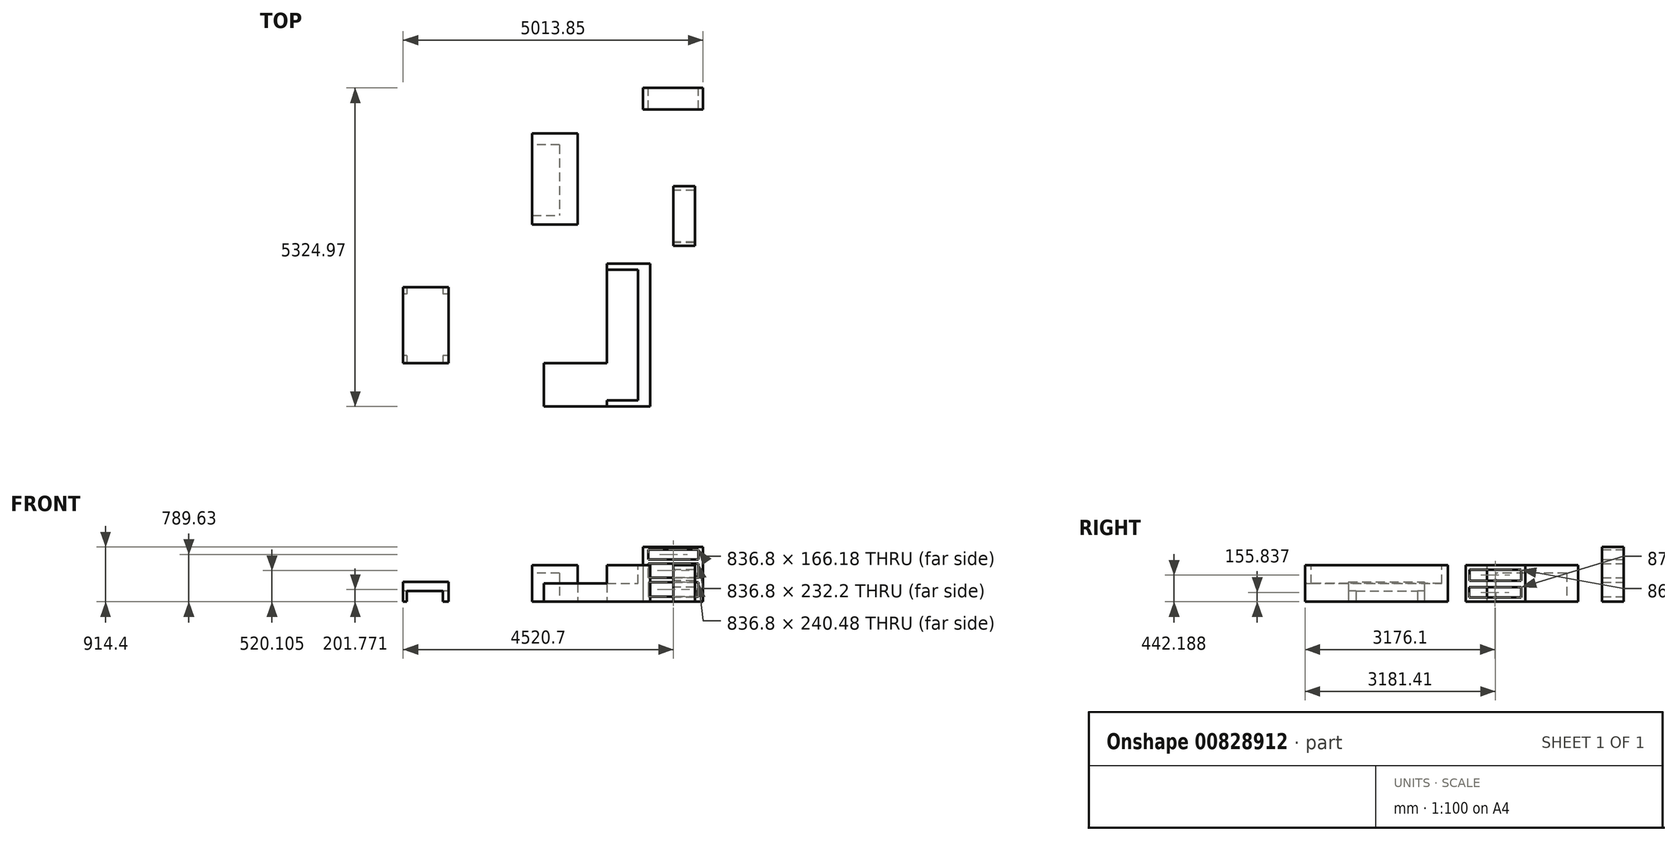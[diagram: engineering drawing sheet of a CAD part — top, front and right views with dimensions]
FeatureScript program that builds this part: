
annotation { "Feature Type Name" : "Feature", "Feature Type Description" : "" }
export const myFeature = defineFeature(function(context is Context, id is Id, definition is map)
    precondition{}
    {
        {
            var Q0;
            Q0=qCreatedBy(makeId("Top.planeOp"),FACE);
            var sketch = newSketch(context, id + "F0", { "sketchPlane" : qUnion([Q0])});
            skLineSegment(sketch, "E0", {"start": v(0, 0) * mm, "end": v(0, -723.9) * mm});
            skLineSegment(sketch, "E1", {"start": v(0, -723.9) * mm, "end": v(1778, -723.9) * mm});
            skLineSegment(sketch, "E2", {"start": v(1778, -723.9) * mm, "end": v(1778, 1663.7) * mm});
            skLineSegment(sketch, "E3", {"start": v(1778, 1663.7) * mm, "end": v(1054.1, 1663.7) * mm});
            skLineSegment(sketch, "E4", {"start": v(1054.1, 1663.7) * mm, "end": v(1054.1, 0) * mm});
            skLineSegment(sketch, "E5", {"start": v(1054.1, 0) * mm, "end": v(0, 0) * mm});
            skSolve(sketch);
        }
        {
            var Q0;
            Q0 = qSketchRegion(id + "F0", true);
            extrude(context, id + "F1", {"entities" : qUnion([Q0]), "depth" : 609.6 * mm, "offsetDistance" : 25.4 * mm});
        }
        {
            var Q0;
            Q0=makeQuery(id+"F1.opExtrude","CAP_FACE",FACE,{"disambiguationData":[OSD([sQuery(id+"F0.wireOp",EDGE,"E0"),sQuery(id+"F0.wireOp",EDGE,"E1"),sQuery(id+"F0.wireOp",EDGE,"E2"),sQuery(id+"F0.wireOp",EDGE,"E3"),sQuery(id+"F0.wireOp",EDGE,"E4"),sQuery(id+"F0.wireOp",EDGE,"E5")])],"isStart":false});
            var sketch = newSketch(context, id + "F2", { "sketchPlane" : qUnion([Q0])});
            skLineSegment(sketch, "E6", {"start": v(1054.1, -723.9) * mm, "end": v(1054.1, -622.3) * mm});
            skLineSegment(sketch, "E7", {"start": v(1054.1, -622.3) * mm, "end": v(1574.8, -622.3) * mm});
            skLineSegment(sketch, "E8", {"start": v(1574.8, -622.3) * mm, "end": v(1574.8, 1562.1) * mm});
            skLineSegment(sketch, "E9", {"start": v(1054.1, 0) * mm, "end": v(0, 0) * mm});
            skLineSegment(sketch, "E10", {"start": v(0, 0) * mm, "end": v(0, -723.9) * mm});
            skLineSegment(sketch, "E11", {"start": v(0, -723.9) * mm, "end": v(1054.1, -723.9) * mm});
            skLineSegment(sketch, "E12", {"start": v(1574.8, 1562.1) * mm, "end": v(1054.1, 1562.1) * mm});
            skLineSegment(sketch, "E13", {"start": v(1054.1, 0) * mm, "end": v(1054.1, 1562.1) * mm});
            skSolve(sketch);
        }
        {
            var Q0;
            Q0 = qSketchRegion(id + "F2", true);
            extrude(context, id + "F3", {"entities" : qUnion([Q0]), "operationType" : NewBodyOperationType.REMOVE, "oppositeDirection" : true, "depth" : 304.8 * mm, "offsetDistance" : 25.4 * mm});
        }
        {
            var Q0;
            Q0=qCreatedBy(makeId("Top.planeOp"),FACE);
            var sketch = newSketch(context, id + "F4", { "sketchPlane" : qUnion([Q0])});
            skLineSegment(sketch, "E14.bottom", {"start": v(-2356.13, 0) * mm, "end": v(-1594.13, 0) * mm});
            skLineSegment(sketch, "E14.top", {"start": v(-2356.13, 1270) * mm, "end": v(-1594.13, 1270) * mm});
            skLineSegment(sketch, "E14.left", {"start": v(-2356.13, 0) * mm, "end": v(-2356.13, 1270) * mm});
            skLineSegment(sketch, "E14.right", {"start": v(-1594.13, 0) * mm, "end": v(-1594.13, 1270) * mm});
            skSolve(sketch);
        }
        {
            var Q0;
            Q0 = qSketchRegion(id + "F4", true);
            extrude(context, id + "F5", {"entities" : qUnion([Q0]), "depth" : 330.2 * mm, "offsetDistance" : 25.4 * mm});
        }
        {
            var Q0;
            Q0=makeQuery(id+"F5.opExtrude","CAP_FACE",FACE,{"disambiguationData":[OSD([sQuery(id+"F4.wireOp",EDGE,"E14.bottom"),sQuery(id+"F4.wireOp",EDGE,"E14.top"),sQuery(id+"F4.wireOp",EDGE,"E14.left"),sQuery(id+"F4.wireOp",EDGE,"E14.right")])],"isStart":true});
            var sketch = newSketch(context, id + "F6", { "sketchPlane" : qUnion([Q0])});
            skLineSegment(sketch, "E15.bottom", {"start": v(-1594.13, -128.71) * mm, "end": v(-1690.59, -128.71) * mm});
            skLineSegment(sketch, "E15.top", {"start": v(-1594.13, -1156.15) * mm, "end": v(-1690.59, -1156.15) * mm});
            skLineSegment(sketch, "E15.left", {"start": v(-1594.13, -128.71) * mm, "end": v(-1594.13, -1156.15) * mm});
            skLineSegment(sketch, "E15.right", {"start": v(-2356.13, -128.71) * mm, "end": v(-2356.13, -1156.15) * mm});
            skLineSegment(sketch, "E16.bottom", {"start": v(-1690.59, -1270) * mm, "end": v(-2293.47, -1270) * mm});
            skLineSegment(sketch, "E16.top", {"start": v(-1690.59, 0) * mm, "end": v(-2293.47, 0) * mm});
            skLineSegment(sketch, "E16.left", {"start": v(-1690.59, -1270) * mm, "end": v(-1690.59, -1156.15) * mm});
            skLineSegment(sketch, "E16.right", {"start": v(-2293.47, -1270) * mm, "end": v(-2293.47, -1156.15) * mm});
            skLineSegment(sketch, "E17.trimOffspring", {"start": v(-1690.59, -128.71) * mm, "end": v(-1690.59, 0) * mm});
            skLineSegment(sketch, "E18.trimOffspring", {"start": v(-2293.47, -128.71) * mm, "end": v(-2356.13, -128.71) * mm});
            skLineSegment(sketch, "E19.trimOffspring", {"start": v(-2293.47, -128.71) * mm, "end": v(-2293.47, 0) * mm});
            skLineSegment(sketch, "E20.trimOffspring", {"start": v(-2293.47, -1156.15) * mm, "end": v(-2356.13, -1156.15) * mm});
            skSolve(sketch);
        }
        {
            var Q0;
            Q0 = qSketchRegion(id + "F6", true);
            extrude(context, id + "F7", {"entities" : qUnion([Q0]), "operationType" : NewBodyOperationType.REMOVE, "oppositeDirection" : true, "depth" : 177.8 * mm, "offsetDistance" : 25.4 * mm});
        }
        {
            var Q0;
            Q0=qCreatedBy(makeId("Top.planeOp"),FACE);
            var sketch = newSketch(context, id + "F8", { "sketchPlane" : qUnion([Q0])});
            skLineSegment(sketch, "E21.bottom", {"start": v(565.89, 2319.93) * mm, "end": v(-1059.71, 2319.93) * mm});
            skLineSegment(sketch, "E21.top", {"start": v(565.89, 3843.93) * mm, "end": v(-196.11, 3843.93) * mm});
            skLineSegment(sketch, "E21.left", {"start": v(565.89, 2319.93) * mm, "end": v(565.89, 3843.93) * mm});
            skLineSegment(sketch, "E21.right", {"start": v(-1059.71, 2319.93) * mm, "end": v(-1059.71, 2878.73) * mm});
            skLineSegment(sketch, "E22.top", {"start": v(-1059.71, 2878.73) * mm, "end": v(-196.11, 2878.73) * mm});
            skLineSegment(sketch, "E22.right", {"start": v(-196.11, 3843.93) * mm, "end": v(-196.11, 2878.73) * mm});
            skSolve(sketch);
        }
        {
            var Q0;
            Q0 = qSketchRegion(id + "F8", true);
            extrude(context, id + "F9", {"entities" : qUnion([Q0]), "depth" : 609.6 * mm, "offsetDistance" : 25.4 * mm});
        }
        {
            var Q0;
            Q0=makeQuery(id+"F9.opExtrude","SWEPT_FACE",FACE,{"disambiguationData":[OSD([sQuery(id+"F8.wireOp",EDGE,"E22.right")])]});
            var sketch = newSketch(context, id + "F10", { "sketchPlane" : qUnion([Q0])});
            skLineSegment(sketch, "E23.bottom", {"start": v(-3650.65, 479.96) * mm, "end": v(-2878.73, 479.96) * mm});
            skLineSegment(sketch, "E23.top", {"start": v(-3650.65, 0) * mm, "end": v(-2878.73, 0) * mm});
            skLineSegment(sketch, "E23.left", {"start": v(-3650.65, 479.96) * mm, "end": v(-3650.65, 0) * mm});
            skLineSegment(sketch, "E23.right", {"start": v(-2878.73, 479.96) * mm, "end": v(-2878.73, 0) * mm});
            skSolve(sketch);
        }
        {
            var Q0;
            Q0 = qSketchRegion(id + "F10", true);
            extrude(context, id + "F11", {"entities" : qUnion([Q0]), "operationType" : NewBodyOperationType.REMOVE, "oppositeDirection" : true, "depth" : 457.2 * mm, "offsetDistance" : 25.4 * mm});
        }
        {
            var Q0;
            Q0=makeQuery(id+"F11.boolean.opBoolean","MERGE",FACE,{"derivedFrom":[makeQuery(id+"F9.opExtrude","SWEPT_FACE",FACE,{"disambiguationData":[OSD([sQuery(id+"F8.wireOp",EDGE,"E22.top")])]}),makeQuery(id+"F11.opExtrude","SWEPT_FACE",FACE,{"disambiguationData":[OSD([sQuery(id+"F10.wireOp",EDGE,"E23.right")])]})]});
            var sketch = newSketch(context, id + "F12", { "sketchPlane" : qUnion([Q0])});
            skLineSegment(sketch, "E24.bottom", {"start": v(-261.09, 479.96) * mm, "end": v(509.69, 479.96) * mm});
            skLineSegment(sketch, "E24.top", {"start": v(-261.09, 0) * mm, "end": v(509.69, 0) * mm});
            skLineSegment(sketch, "E24.left", {"start": v(-261.09, 479.96) * mm, "end": v(-261.09, 0) * mm});
            skLineSegment(sketch, "E24.right", {"start": v(509.69, 479.96) * mm, "end": v(509.69, 0) * mm});
            skSolve(sketch);
        }
        {
            var Q0;
            Q0 = qSketchRegion(id + "F12", true);
            extrude(context, id + "F13", {"entities" : qUnion([Q0]), "operationType" : NewBodyOperationType.REMOVE, "oppositeDirection" : true, "depth" : 406.4 * mm, "offsetDistance" : 25.4 * mm});
        }
        {
            var Q0;
            Q0=qCreatedBy(makeId("Top.planeOp"),FACE);
            var sketch = newSketch(context, id + "F14", { "sketchPlane" : qUnion([Q0])});
            skLineSegment(sketch, "E25.bottom", {"start": v(2657.72, 4242.3) * mm, "end": v(1657.6, 4242.3) * mm});
            skLineSegment(sketch, "E25.left", {"start": v(2657.72, 4242.3) * mm, "end": v(2657.72, 4601.07) * mm});
            skLineSegment(sketch, "E25.right", {"start": v(1657.6, 4242.3) * mm, "end": v(1657.6, 4601.07) * mm});
            skLineSegment(sketch, "E26", {"start": v(2657.72, 4601.07) * mm, "end": v(1657.6, 4601.07) * mm});
            skSolve(sketch);
        }
        {
            var Q0;
            Q0 = qSketchRegion(id + "F14", true);
            extrude(context, id + "F15", {"entities" : qUnion([Q0]), "depth" : 914.4 * mm, "offsetDistance" : 25.4 * mm});
        }
        {
            var Q0;
            Q0=makeQuery(id+"F15.opExtrude","SWEPT_FACE",FACE,{"disambiguationData":[OSD([sQuery(id+"F14.wireOp",EDGE,"E26")])]});
            var sketch = newSketch(context, id + "F16", { "sketchPlane" : qUnion([Q0])});
            skLineSegment(sketch, "E27.bottom", {"start": v(-2582.97, 81.53) * mm, "end": v(-1746.17, 81.53) * mm});
            skLineSegment(sketch, "E27.top", {"start": v(-2582.97, 322) * mm, "end": v(-1746.17, 322) * mm});
            skLineSegment(sketch, "E27.left", {"start": v(-2582.97, 81.53) * mm, "end": v(-2582.97, 322) * mm});
            skLineSegment(sketch, "E27.right", {"start": v(-1746.17, 81.53) * mm, "end": v(-1746.17, 322) * mm});
            skLineSegment(sketch, "E28.bottom", {"start": v(-2582.97, 636.2) * mm, "end": v(-1746.17, 636.2) * mm});
            skLineSegment(sketch, "E28.top", {"start": v(-2582.97, 404) * mm, "end": v(-1746.17, 404) * mm});
            skLineSegment(sketch, "E28.left", {"start": v(-2582.97, 636.2) * mm, "end": v(-2582.97, 404) * mm});
            skLineSegment(sketch, "E28.right", {"start": v(-1746.17, 636.2) * mm, "end": v(-1746.17, 404) * mm});
            skLineSegment(sketch, "E29.bottom", {"start": v(-2582.97, 706.54) * mm, "end": v(-1746.17, 706.54) * mm});
            skLineSegment(sketch, "E29.top", {"start": v(-2582.97, 872.72) * mm, "end": v(-1746.17, 872.72) * mm});
            skLineSegment(sketch, "E29.left", {"start": v(-2582.97, 706.54) * mm, "end": v(-2582.97, 872.72) * mm});
            skLineSegment(sketch, "E29.right", {"start": v(-1746.17, 706.54) * mm, "end": v(-1746.17, 872.72) * mm});
            skSolve(sketch);
        }
        {
            var Q0;
            Q0 = qSketchRegion(id + "F16", true);
            extrude(context, id + "F17", {"entities" : qUnion([Q0]), "operationType" : NewBodyOperationType.REMOVE, "oppositeDirection" : true, "depth" : 381 * mm, "offsetDistance" : 25.4 * mm});
        }
        {
            var Q0;
            Q0=qCreatedBy(makeId("Top.planeOp"),FACE);
            var sketch = newSketch(context, id + "F18", { "sketchPlane" : qUnion([Q0])});
            skLineSegment(sketch, "E30.bottom", {"start": v(2163.1, 2960.16) * mm, "end": v(2521.88, 2960.16) * mm});
            skLineSegment(sketch, "E30.top", {"start": v(2163.1, 1960.03) * mm, "end": v(2521.88, 1960.03) * mm});
            skLineSegment(sketch, "E30.left", {"start": v(2163.1, 2960.16) * mm, "end": v(2163.1, 1960.03) * mm});
            skLineSegment(sketch, "E30.right", {"start": v(2521.88, 2960.16) * mm, "end": v(2521.88, 1960.03) * mm});
            skSolve(sketch);
        }
        {
            var Q0;
            Q0 = qSketchRegion(id + "F18", true);
            extrude(context, id + "F19", {"entities" : qUnion([Q0]), "depth" : 609.6 * mm, "offsetDistance" : 25.4 * mm});
        }
        {
            var Q0;
            Q0=makeQuery(id+"F19.opExtrude","SWEPT_FACE",FACE,{"disambiguationData":[OSD([sQuery(id+"F18.wireOp",EDGE,"E30.left")])]});
            var sketch = newSketch(context, id + "F20", { "sketchPlane" : qUnion([Q0])});
            skLineSegment(sketch, "E31.bottom", {"start": v(-2890.59, 533.26) * mm, "end": v(-2024.44, 533.26) * mm});
            skLineSegment(sketch, "E31.top", {"start": v(-2890.59, 351.11) * mm, "end": v(-2024.44, 351.11) * mm});
            skLineSegment(sketch, "E31.left", {"start": v(-2890.59, 533.26) * mm, "end": v(-2890.59, 351.11) * mm});
            skLineSegment(sketch, "E31.right", {"start": v(-2024.44, 533.26) * mm, "end": v(-2024.44, 351.11) * mm});
            skLineSegment(sketch, "E32.bottom", {"start": v(-2888.3, 240.22) * mm, "end": v(-2016.1, 240.22) * mm});
            skLineSegment(sketch, "E32.top", {"start": v(-2888.3, 71.45) * mm, "end": v(-2016.1, 71.45) * mm});
            skLineSegment(sketch, "E32.left", {"start": v(-2888.3, 240.22) * mm, "end": v(-2888.3, 71.45) * mm});
            skLineSegment(sketch, "E32.right", {"start": v(-2016.1, 240.22) * mm, "end": v(-2016.1, 71.45) * mm});
            skSolve(sketch);
        }
        {
            var Q0;
            Q0 = qSketchRegion(id + "F20", true);
            extrude(context, id + "F21", {"entities" : qUnion([Q0]), "operationType" : NewBodyOperationType.REMOVE, "oppositeDirection" : true, "depth" : 381 * mm, "offsetDistance" : 25.4 * mm});
        }
        {
            var Q0;
            Q0=makeQuery(id+"F9.opExtrude","CAP_FACE",FACE,{"disambiguationData":[OSD([sQuery(id+"F8.wireOp",EDGE,"E21.bottom"),sQuery(id+"F8.wireOp",EDGE,"E21.top"),sQuery(id+"F8.wireOp",EDGE,"E21.left"),sQuery(id+"F8.wireOp",EDGE,"E21.right"),sQuery(id+"F8.wireOp",EDGE,"E22.top"),sQuery(id+"F8.wireOp",EDGE,"E22.right")])],"isStart":false});
            var sketch = newSketch(context, id + "F22", { "sketchPlane" : qUnion([Q0])});
            skLineSegment(sketch, "E33.bottom", {"start": v(-1059.71, 2878.73) * mm, "end": v(-196.11, 2878.73) * mm});
            skLineSegment(sketch, "E33.top", {"start": v(-1059.71, 2319.93) * mm, "end": v(-196.11, 2319.93) * mm});
            skLineSegment(sketch, "E33.left", {"start": v(-1059.71, 2878.73) * mm, "end": v(-1059.71, 2319.93) * mm});
            skLineSegment(sketch, "E33.right", {"start": v(-196.11, 2878.73) * mm, "end": v(-196.11, 2319.93) * mm});
            skSolve(sketch);
        }
        {
            var Q0;
            Q0 = qSketchRegion(id + "F22", true);
            extrude(context, id + "F23", {"entities" : qUnion([Q0]), "operationType" : NewBodyOperationType.REMOVE, "endBound" : BoundingType.THROUGH_ALL, "oppositeDirection" : true, "depth" : 25.4 * mm, "offsetDistance" : 25.4 * mm});
        }
    });
